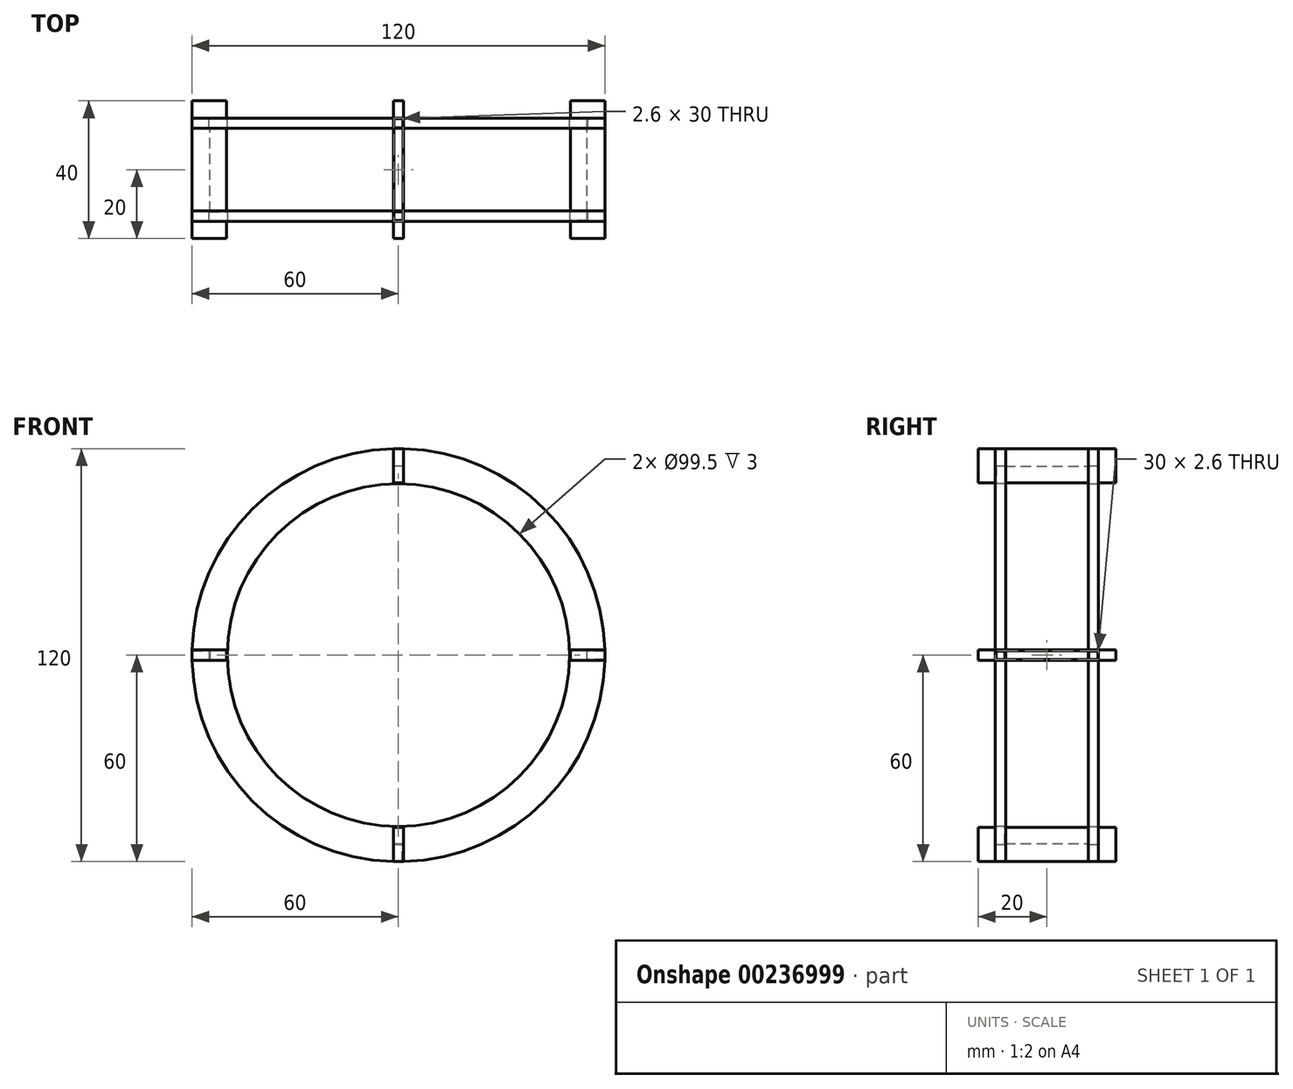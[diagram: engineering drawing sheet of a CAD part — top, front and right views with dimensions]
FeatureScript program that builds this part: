
annotation { "Feature Type Name" : "Feature", "Feature Type Description" : "" }
export const myFeature = defineFeature(function(context is Context, id is Id, definition is map)
    precondition{}
    {
        {
            var Q0;
            Q0=qCreatedBy(makeId("Front.planeOp"),FACE);
            var sketch = newSketch(context, id + "F0", { "sketchPlane" : qUnion([Q0])});
            skCircle(sketch, "E0", {"center": v(0, 0) * mm, "radius": 49.75 * mm});
            skCircle(sketch, "E1", {"center": v(0, 0) * mm, "radius": 60 * mm});
            skSolve(sketch);
        }
        {
            var Q0;
            Q0=qCreatedBy(makeId("Front.planeOp"),FACE);
            cPlane(context, id + "F1", {"entities" : qUnion([Q0]), "cplaneType" : CPlaneType.OFFSET, "offset" : 30 * mm, "width" : 150 * mm, "height" : 150 * mm});
        }
        {
            var Q0;
            Q0=qCreatedBy(id+"F1.planeOp",FACE);
            var sketch = newSketch(context, id + "F2", { "sketchPlane" : qUnion([Q0])});
            skCircle(sketch, "E2", {"center": v(0, 0) * mm, "radius": 49.75 * mm});
            skCircle(sketch, "E3", {"center": v(0, 0) * mm, "radius": 60 * mm});
            skSolve(sketch);
        }
        {
            var Q0;
            Q0=qCreatedBy(makeId("Right.planeOp"),FACE);
            var sketch = newSketch(context, id + "F3", { "sketchPlane" : qUnion([Q0])});
            skLineSegment(sketch, "E4.bottom", {"start": v(-35, 60) * mm, "end": v(5, 60) * mm});
            skLineSegment(sketch, "E4.top", {"start": v(-35, 50) * mm, "end": v(5, 50) * mm});
            skLineSegment(sketch, "E4.left", {"start": v(-35, 60) * mm, "end": v(-35, 50) * mm});
            skLineSegment(sketch, "E4.right", {"start": v(5, 60) * mm, "end": v(5, 50) * mm});
            skSolve(sketch);
        }
        {
            var Q0;
            Q0=makeQuery(id+"F0.imprint","IMPRINT",FACE,{"disambiguationData":[TD([[makeQuery(id+"F0.imprint","IMPRINT",EDGE,{"derivedFrom":sQuery(id+"F0.wireOp",EDGE,"E0")}),-1.0]])]});
            extrude(context, id + "F4", {"entities" : qUnion([Q0]), "depth" : 3 * mm});
        }
        {
            var Q0;
            Q0=makeQuery(id+"F2.imprint","IMPRINT",FACE,{"disambiguationData":[TD([[makeQuery(id+"F2.imprint","IMPRINT",EDGE,{"derivedFrom":sQuery(id+"F2.wireOp",EDGE,"E2")}),-1.0]])]});
            extrude(context, id + "F5", {"entities" : qUnion([Q0]), "oppositeDirection" : true, "depth" : 3 * mm});
        }
        {
            var Q0;
            Q0=makeQuery(id+"F3.imprint","IMPRINT",FACE,{"disambiguationData":[TD([[makeQuery(id+"F3.imprint","IMPRINT",EDGE,{"derivedFrom":sQuery(id+"F3.wireOp",EDGE,"E4.bottom")}),-1.0]])]});
            var Q1;
            Q1=makeQuery(id+"F3.imprint","IMPRINT",FACE,{"disambiguationData":[TD([[makeQuery(id+"F3.imprint","IMPRINT",EDGE,{"derivedFrom":sQuery(id+"F3.wireOp",EDGE,"af6e27a3-cd48-4d8d-b3ba-524074a455990.MirrorCS")}),1.0]])]});
            extrude(context, id + "F6", {"entities" : qUnion([Q0, Q1]), "depth" : 1.5 * mm, "hasSecondDirection" : true, "secondDirectionOppositeDirection" : true, "secondDirectionDepth" : 1.5 * mm});
        }
        {
            var Q0;
            Q0=qCreatedBy(makeId("Front.planeOp"),FACE);
            var sketch = newSketch(context, id + "F7", { "sketchPlane" : qUnion([Q0])});
            skLineSegment(sketch, "E5", {"start": v(0, 68) * mm, "end": v(0, -74.52) * mm, "construction": true});
            skLineSegment(sketch, "E6", {"start": v(-72.99, 0) * mm, "end": v(86.59, 0) * mm, "construction": true});
            skLineSegment(sketch, "E7.bottom", {"start": v(1.3, 61.8) * mm, "end": v(-1.3, 61.8) * mm});
            skLineSegment(sketch, "E7.top", {"start": v(1.3, 54.8) * mm, "end": v(-1.3, 54.8) * mm});
            skLineSegment(sketch, "E7.left", {"start": v(1.3, 61.8) * mm, "end": v(1.3, 54.8) * mm});
            skLineSegment(sketch, "E7.right", {"start": v(-1.3, 61.8) * mm, "end": v(-1.3, 54.8) * mm});
            skPoint(sketch, "E7.middle", {"position": v(0, 58.3) * mm});
            skLineSegment(sketch, "E8.1.0", {"start": v(-62, 1.3) * mm, "end": v(-62, -1.3) * mm});
            skLineSegment(sketch, "E8.1.1", {"start": v(-62, 1.3) * mm, "end": v(-55, 1.3) * mm});
            skLineSegment(sketch, "E8.1.2", {"start": v(-55, 1.3) * mm, "end": v(-55, -1.3) * mm});
            skLineSegment(sketch, "E8.1.3", {"start": v(-62, -1.3) * mm, "end": v(-55, -1.3) * mm});
            skLineSegment(sketch, "E8.2.0", {"start": v(-1.5, -62) * mm, "end": v(1.1, -62) * mm});
            skLineSegment(sketch, "E8.2.1", {"start": v(-1.5, -62) * mm, "end": v(-1.5, -55) * mm});
            skLineSegment(sketch, "E8.2.2", {"start": v(-1.5, -55) * mm, "end": v(1.1, -55) * mm});
            skLineSegment(sketch, "E8.2.3", {"start": v(1.1, -62) * mm, "end": v(1.1, -55) * mm});
            skLineSegment(sketch, "E8.3.0", {"start": v(61.8, -1.5) * mm, "end": v(61.8, 1.1) * mm});
            skLineSegment(sketch, "E8.3.1", {"start": v(61.8, -1.5) * mm, "end": v(54.8, -1.5) * mm});
            skLineSegment(sketch, "E8.3.2", {"start": v(54.8, -1.5) * mm, "end": v(54.8, 1.1) * mm});
            skLineSegment(sketch, "E8.3.3", {"start": v(61.8, 1.1) * mm, "end": v(54.8, 1.1) * mm});
            skPoint(sketch, "E8.center", {"position": v(-0.1, -0.1) * mm});
            skSolve(sketch);
        }
        {
            var Q0;
            Q0 = qSketchRegion(id + "F7", true);
            extrude(context, id + "F8", {"entities" : qUnion([Q0]), "operationType" : NewBodyOperationType.REMOVE, "depth" : 30 * mm});
        }
        {
            var Q0;
            Q0=makeQuery(id+"F6.opExtrude","CAP_FACE",FACE,{"disambiguationData":[OSD([sQuery(id+"F3.wireOp",EDGE,"E4.bottom"),sQuery(id+"F3.wireOp",EDGE,"E4.top"),sQuery(id+"F3.wireOp",EDGE,"E4.left"),sQuery(id+"F3.wireOp",EDGE,"E4.right")])],"isStart":false});
            var sketch = newSketch(context, id + "F9", { "sketchPlane" : qUnion([Q0])});
            skLineSegment(sketch, "E9.bottom", {"start": v(-2.8, 55) * mm, "end": v(-0.2, 55) * mm});
            skLineSegment(sketch, "E9.top", {"start": v(-2.8, 48) * mm, "end": v(-0.2, 48) * mm});
            skLineSegment(sketch, "E9.left", {"start": v(-2.8, 55) * mm, "end": v(-2.8, 48) * mm});
            skLineSegment(sketch, "E9.right", {"start": v(-0.2, 55) * mm, "end": v(-0.2, 48) * mm});
            skLineSegment(sketch, "E10.bottom", {"start": v(-29.8, 55) * mm, "end": v(-27.2, 55) * mm});
            skLineSegment(sketch, "E10.top", {"start": v(-29.8, 48) * mm, "end": v(-27.2, 48) * mm});
            skLineSegment(sketch, "E10.left", {"start": v(-29.8, 55) * mm, "end": v(-29.8, 48) * mm});
            skLineSegment(sketch, "E10.right", {"start": v(-27.2, 55) * mm, "end": v(-27.2, 48) * mm});
            skSolve(sketch);
        }
        {
            var Q0;
            Q0 = qSketchRegion(id + "F9", true);
            extrude(context, id + "F10", {"entities" : qUnion([Q0]), "operationType" : NewBodyOperationType.REMOVE, "oppositeDirection" : true, "depth" : 3 * mm});
        }
        {
            var Q0;
            Q0=makeQuery(id+"F6.opExtrude","SWEPT_BODY",BODY,{"disambiguationData":[OSD([sQuery(id+"F3.wireOp",EDGE,"E4.bottom"),sQuery(id+"F3.wireOp",EDGE,"E4.top"),sQuery(id+"F3.wireOp",EDGE,"E4.left"),sQuery(id+"F3.wireOp",EDGE,"E4.right")])]});
            var Q1;
            Q1=makeQuery(id+"F5.opExtrude","CAP_EDGE",EDGE,{"disambiguationData":[OSD([sQuery(id+"F2.wireOp",EDGE,"E2")])],"isStart":true});
            circularPattern(context, id + "F11", {"entities" : qUnion([Q0]), "axis" : qUnion([Q1]), "angle" : 360 * degree, "instanceCount" : 4, "equalSpace" : true});
        }
    });
